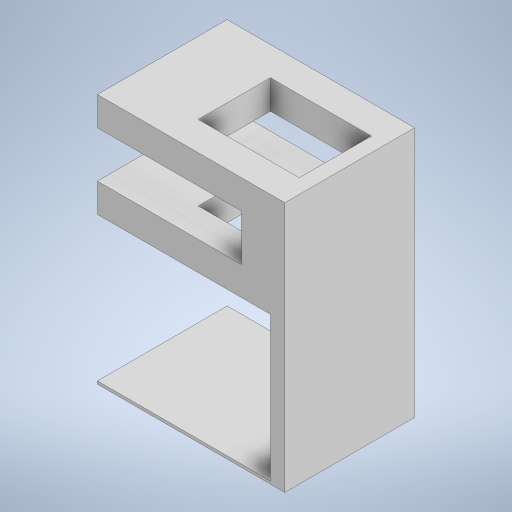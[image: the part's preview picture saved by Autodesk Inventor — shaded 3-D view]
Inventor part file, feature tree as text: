
AUTODESK INVENTOR PART (.ipt)
format: ipt  version: 2023 (Build 270158000, 158)  size: 283,136 bytes
history: native  units: mm
features: extrude x7, sketch x7, other x1
ambient origin geometry x8: Origin, YZ Plane, XZ Plane, XY Plane, X Axis, Y Axis, Z Axis, Center Point
bodies: Body1 (feature_tree)
feature tree (15):
  other  "Твердое тело1"
  extrude  "Выдавливание1"  Depth=60.0mm
  extrude  "Выдавливание3"  Depth=45.0mm
  extrude  "Выдавливание4"  Depth=10.0mm
  extrude  "Выдавливание5"  Depth=35.0mm
  extrude  "Выдавливание6"  Depth=25.0mm
  extrude  "Выдавливание7"  Depth=10.0mm
  extrude  "Выдавливание8"  Depth=10.0mm TaperAngle=0.0deg
  sketch  "Эскиз1"
  sketch  "Эскиз3"
  sketch  "Эскиз4"
  sketch  "Эскиз5"
  sketch  "Эскиз6"
  sketch  "Эскиз7"
  sketch  "Эскиз8"
